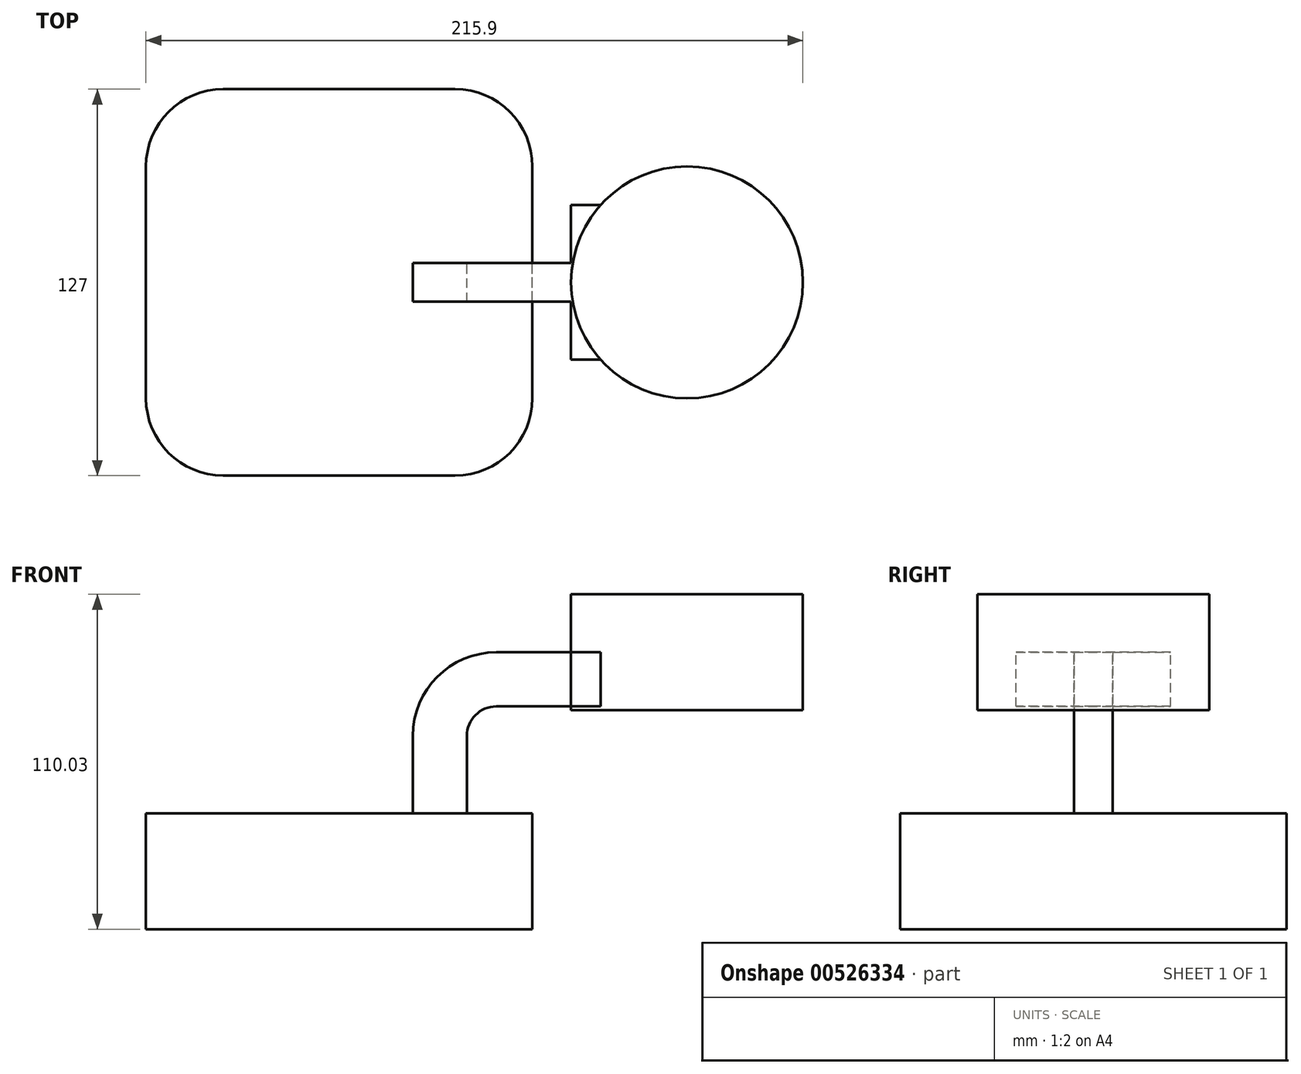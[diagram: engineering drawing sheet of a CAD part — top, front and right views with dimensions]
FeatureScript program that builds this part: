
annotation { "Feature Type Name" : "Feature", "Feature Type Description" : "" }
export const myFeature = defineFeature(function(context is Context, id is Id, definition is map)
    precondition{}
    {
        {
            var Q0;
            Q0=qCreatedBy(makeId("Front.planeOp"),FACE);
            var sketch = newSketch(context, id + "F0", { "sketchPlane" : qUnion([Q0])});
            skLineSegment(sketch, "E0.bottom", {"start": v(63.5, 19.05) * mm, "end": v(-63.5, 19.05) * mm});
            skLineSegment(sketch, "E0.top", {"start": v(63.5, -19.05) * mm, "end": v(-63.5, -19.05) * mm});
            skLineSegment(sketch, "E0.left", {"start": v(63.5, 19.05) * mm, "end": v(63.5, -19.05) * mm});
            skLineSegment(sketch, "E0.right", {"start": v(-63.5, 19.05) * mm, "end": v(-63.5, -19.05) * mm});
            skPoint(sketch, "E0.middle", {"position": v(0, 0) * mm});
            skPoint(sketch, "E1.middle", {"position": v(114.3, 71.93) * mm});
            skLineSegment(sketch, "E2", {"start": v(41.95, -5.7) * mm, "end": v(41.95, 44.45) * mm});
            skArc(sketch, "E3", {"start": v(41.95, 44.45) * mm, "mid": v(44.8, 51.3) * mm, "end": v(51.65, 54.15) * mm});
            skLineSegment(sketch, "E4", {"start": v(51.65, 54.15) * mm, "end": v(114.3, 54.15) * mm});
            skLineSegment(sketch, "E5.0", {"start": v(51.65, 71.93) * mm, "end": v(114.3, 71.93) * mm});
            skArc(sketch, "E5.1", {"start": v(24.17, 44.45) * mm, "mid": v(32.22, 63.88) * mm, "end": v(51.65, 71.93) * mm});
            skLineSegment(sketch, "E5.2", {"start": v(24.17, -5.7) * mm, "end": v(24.17, 44.45) * mm});
            skFitSpline(sketch, "E6", {"points": [v(-63.5, 19.05) * mm, v(51.65, 71.93) * mm], "startDerivative": vector(4.75, 160.35) * mm, "endDerivative": vector(145.91, -1.55) * mm});
            skLineSegment(sketch, "E7", {"start": v(114.3, 71.93) * mm, "end": v(114.3, 54.15) * mm});
            skLineSegment(sketch, "E8.bottom", {"start": v(152.4, 52.88) * mm, "end": v(76.2, 52.88) * mm});
            skLineSegment(sketch, "E8.top", {"start": v(152.4, 90.98) * mm, "end": v(76.2, 90.98) * mm});
            skLineSegment(sketch, "E8.left", {"start": v(152.4, 52.88) * mm, "end": v(152.4, 90.98) * mm});
            skLineSegment(sketch, "E8.right", {"start": v(76.2, 52.88) * mm, "end": v(76.2, 90.98) * mm});
            skLineSegment(sketch, "E9", {"start": v(114.3, 52.88) * mm, "end": v(114.3, 90.98) * mm});
            skSolve(sketch);
        }
        {
            var Q0;
            Q0=makeQuery(id+"F0.imprint","IMPRINT",FACE,{"disambiguationData":[TD([[makeQuery(id+"F0.imprint","IMPRINT",EDGE,{"derivedFrom":sQuery(id+"F0.wireOp",EDGE,"E0.top")}),-1.0]])]});
            extrude(context, id + "F1", {"entities" : qUnion([Q0]), "endBound" : BoundingType.SYMMETRIC, "depth" : 127 * mm, "offsetDistance" : 25.4 * mm});
        }
        {
            var Q0;
            {var subQ4=sQuery(id+"F0.wireOp",EDGE,"E5.1");Q0=makeQuery(id+"F0.imprint","IMPRINT",FACE,{"disambiguationData":[TD([[makeQuery(id+"F0.imprint","IMPRINT",EDGE,{"derivedFrom":subQ4}),1.0]])]});}
            extrude(context, id + "F2", {"entities" : qUnion([Q0]), "operationType" : NewBodyOperationType.ADD, "endBound" : BoundingType.SYMMETRIC, "depth" : 12.7 * mm, "offsetDistance" : 25.4 * mm});
        }
        {
            var Q0;
            {var subQ1=sQuery(id+"F0.wireOp",EDGE,"E3");Q0=makeQuery(id+"F0.imprint","IMPRINT",FACE,{"disambiguationData":[TD([[makeQuery(id+"F0.imprint","IMPRINT",EDGE,{"derivedFrom":subQ1}),1.0]])]});}
            var Q1;
            {var subQ0=sQuery(id+"F0.wireOp",EDGE,"E7");Q1=makeQuery(id+"F0.imprint","IMPRINT",FACE,{"disambiguationData":[TD([[makeQuery(id+"F0.imprint","IMPRINT",EDGE,{"derivedFrom":subQ0}),-1.0]])]});}
            var Q2;
            {var subQ0=sQuery(id+"F0.wireOp",EDGE,"E9");var subQ1=sQuery(id+"F0.wireOp",EDGE,"E4");var subQ2=makeQuery(id+"F0.imprint","INTERSECT",VERTEX,{"derivedFrom":[subQ1,subQ0]});Q2=makeQuery(id+"F0.imprint","IMPRINT",FACE,{"disambiguationData":[TD([[makeQuery(id+"F0.imprint","IMPRINT",EDGE,{"disambiguationData":[TD([[subQ2,1.0]])],"derivedFrom":subQ1}),1.0]])]});}
            extrude(context, id + "F3", {"entities" : qUnion([Q0, Q1, Q2]), "operationType" : NewBodyOperationType.ADD, "endBound" : BoundingType.SYMMETRIC, "depth" : 50.8 * mm, "offsetDistance" : 25.4 * mm});
        }
        {
            var Q0;
            {var subQ4=sQuery(id+"F0.wireOp",EDGE,"E8.left");Q0=makeQuery(id+"F0.imprint","IMPRINT",FACE,{"disambiguationData":[TD([[makeQuery(id+"F0.imprint","IMPRINT",EDGE,{"derivedFrom":subQ4}),1.0]])]});}
            var Q1;
            Q1=sQuery(id+"F0.wireOp",EDGE,"E9");
            revolve(context, id + "F4", {"operationType" : NewBodyOperationType.ADD, "entities" : qUnion([Q0]), "axis" : qUnion([Q1]), "revolveType" : RevolveType.FULL});
        }
        {
            var Q0;
            Q0=makeQuery(id+"F1.opExtrude","CAP_EDGE",EDGE,{"disambiguationData":[OSD([sQuery(id+"F0.wireOp",EDGE,"E0.right")])],"isStart":false});
            var Q1;
            Q1=makeQuery(id+"F1.opExtrude","CAP_EDGE",EDGE,{"disambiguationData":[OSD([sQuery(id+"F0.wireOp",EDGE,"E0.left")])],"isStart":false});
            var Q2;
            Q2=makeQuery(id+"F1.opExtrude","CAP_EDGE",EDGE,{"disambiguationData":[OSD([sQuery(id+"F0.wireOp",EDGE,"E0.right")])],"isStart":true});
            var Q3;
            Q3=makeQuery(id+"F1.opExtrude","CAP_EDGE",EDGE,{"disambiguationData":[OSD([sQuery(id+"F0.wireOp",EDGE,"E0.left")])],"isStart":true});
            fillet(context, id + "F5", {"entities" : qUnion([Q0, Q1, Q2, Q3]), "radius" : 25.4 * mm, "tangentPropagation" : true, "allowEdgeOverflow" : false});
        }
    });
